# Revit family: P190780JX-075c_JBRFR36IGX_Refrigeration_Columns
name_source: partatom
category: Specialty Equipment
units: mm (PartAtom-declared; Revit-internal decimal feet)

## family parameters
Always vertical = Yes
Cut with Voids When Loaded = No
Enable Cutting in Views = No
Maintain Annotation Orientation = No
Part Type = Normal
Room Calculation Point = No
Round Connector Dimension = Use Diameter
Shared = No
Work Plane-Based = No

## types (1)
- JBRFR36IGX
    Accent Material = ARCAT - Metal - Steel - Black
    Amps = 0 A
    Body Material = ARCAT - Metal - Steel - Stainless
    Clearance Material = ARCAT - Clearance
    Default Elevation = 0"
    Depth = 27 1/8"
    Description = 36” Built-In Refrigerator Column (Right-Hand Door Swing)
Colonne de réfrigération encastrée prête pour le panneau de recouvrement, charnières à droite, 36 po
    Dimension Guide = http://access.whirlpool.com
    Door Material = ARCAT - Thermal - Wood Fiber Cover Board
    Energy Guide = http://access.whirlpool.com Guide&sku=JBRFR36IGX&language=EN
    Family Name = 36" BIR (right hand)
    Feature 1 = Over 250 Configurations
Plus de 250 configurations
    Feature 2 = Trinity Cooling
Refroidissement triple
    Feature 3 = Remote Access
Accès à distance
    Handle Material = ARCAT - Metal - Steel - Stainless
    Height = 79 7/8"
    Installation-Fabrication = https://www.whirlpool.com
    Manufacturer = Jenn Air
    Model = JBRFR36IGX
    Voltage = 0 V
    Wheel Material = ARCAT - Plastic - Black
    Width = 35 3/4"

## geometry (parser evidence)
native form markers: Sweep x3
no freeform markers — native parametric forms only
